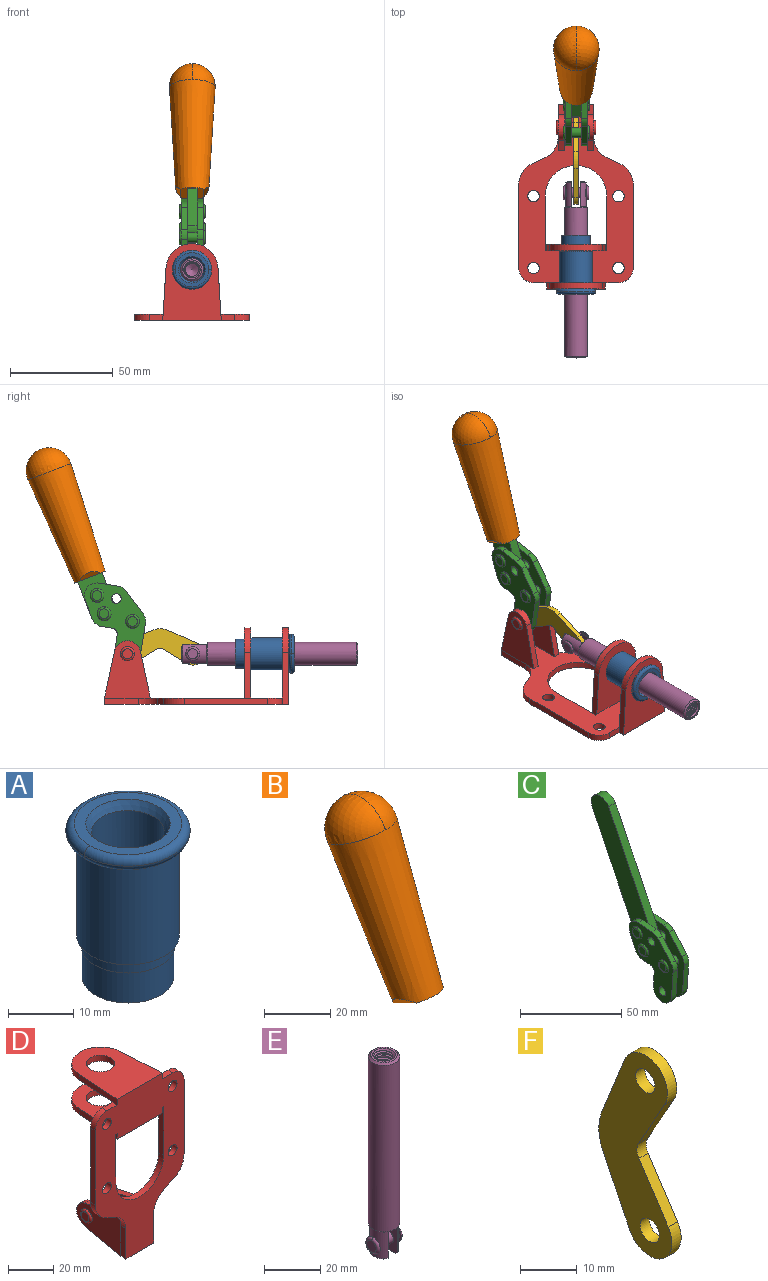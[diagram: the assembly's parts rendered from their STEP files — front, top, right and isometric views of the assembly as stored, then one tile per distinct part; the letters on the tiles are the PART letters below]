
ASSEMBLY  parts=6 mates=6
PART A: 15 faces, bbox 20.6x20.6x28.7 mm
  f0: torus R=8.26mm, axis (0,0,1), area 56.8mm2, adj f1,f10,f12
  f1: torus R=8.26mm, axis (0,0,1), area 56.8mm2, adj f0,f6,f13
  f2: cylinder r=5.59mm len=25.91mm, axis (0,0,1), area 909.6mm2, adj f3,f4
  f3: cone r=6.86mm half-angle=45deg, axis (0,0,-1), area 70.2mm2, adj f2,f14
  f4: cone r=6.47mm half-angle=30deg, axis (0,0,1), area 66.7mm2, adj f2,f13
  f5: cylinder r=7.04mm len=14.07mm, axis (0,0,1), area 252.6mm2, adj f11,f14
  f6: torus R=8.26mm, axis (0,0,1), area 56.8mm2, adj f1,f12,f13
  f7: cylinder r=7.16mm len=14.33mm, axis (0,0,1), area 91.5mm2, adj f9,f11
  f8: cylinder r=7.86mm len=18.42mm, axis (0,0,1), area 909.6mm2, adj f9,f10
  f9: plane 15.72x15.72mm, normal (0,0,-1), area 33mm2, adj f7,f8
  f10: plane 16.51x16.51mm, normal (0,0,-1), area 19.9mm2, adj f0,f8,f12
  f11: plane 14.33x14.33mm, normal (0,0,-1), area 5.7mm2, adj f5,f7
  f12: torus R=8.26mm, axis (0,0,1), area 56.8mm2, adj f0,f6,f10
  f13: plane 16.51x16.51mm, normal (0,0,1), area 82.7mm2, adj f1,f4,f6
  f14: plane 14.07x14.07mm, normal (0,0,-1), area 7.8mm2, adj f3,f5
PART B: 11 faces, bbox 22.3x42.6x64.5 mm
  f0: sphere r=11.13mm, area 411.4mm2, adj f1,f8
  f1: cone r=11.11mm half-angle=3.3deg, axis (0,0.44,0.9), area 3251.8mm2, adj f0,f7,f8,f9,f10
  f2: cylinder r=6.16mm len=11.7mm, axis (1,0,0), area 89.5mm2, adj f3,f4,f5,f6
  f3: plane 60.23x36.75mm, normal (-1,0,0), area 763.6mm2, adj f2,f4,f6,f10
  f4: plane 51.37x25.05mm, normal (0,0.9,-0.44), area 264.2mm2, adj f2,f3,f5,f10
  f5: plane 60.23x36.75mm, normal (1,0,0), area 763.6mm2, adj f2,f4,f6,f10
  f6: plane 51.37x25.05mm, normal (0,-0.9,0.44), area 264.2mm2, adj f2,f3,f5,f10
  f7: plane 9.95x5.95mm, normal (0.71,-0.31,-0.64), area 25.8mm2, adj f1,f10
  f8: sphere r=11.13mm, area 411.4mm2, adj f0,f1
  f9: plane 9.95x5.95mm, normal (-0.71,-0.31,-0.64), area 25.8mm2, adj f1,f10
  f10: plane 14.27x11.38mm, normal (0,-0.44,-0.9), area 106.7mm2, adj f1,f3,f4,f5,f6,f7,f9
PART C: 59 faces, bbox 12.9x60.2x99.6 mm
  f0: torus R=2.39mm, axis (-1,0,0), area 14.9mm2, adj f20,f43,f51
  f1: torus R=2.39mm, axis (-1,0,0), area 14.9mm2, adj f19,f42,f51
  f2: torus R=2.39mm, axis (-1,0,0), area 14.9mm2, adj f18,f35,f51
  f3: torus R=2.39mm, axis (-1,0,0), area 14.9mm2, adj f14,f17,f23
  f4: torus R=2.39mm, axis (-1,0,0), area 14.9mm2, adj f13,f16,f23
  f5: torus R=2.39mm, axis (-1,0,0), area 14.9mm2, adj f12,f15,f23
  f6: cylinder r=2.39mm len=4.78mm, axis (1,0,0), area 46.5mm2, adj f48,f50,f51
  f7: cylinder r=2.39mm len=4.78mm, axis (1,0,0), area 46.5mm2, adj f50,f51
  f8: cylinder r=6.35mm len=12.68mm, axis (1,0,0), area 61.8mm2, adj f38,f39,f50,f51
  f9: cylinder r=2.39mm len=4.78mm, axis (-1,0,0), area 70.5mm2, adj f46,f50
  f10: cylinder r=2.39mm len=4.78mm, axis (-1,0,0), area 46.5mm2, adj f23,f45,f46
  f11: cylinder r=2.39mm len=4.78mm, axis (-1,0,0), area 46.5mm2, adj f23,f46
  f12: plane 4.78x4.78mm, normal (1,0,0), area 17.9mm2, adj f5,f15
  f13: plane 4.78x4.78mm, normal (1,0,0), area 17.9mm2, adj f4,f16
  f14: plane 4.78x4.78mm, normal (1,0,0), area 17.9mm2, adj f3,f17
  f15: torus R=2.39mm, axis (-1,0,0), area 14.9mm2, adj f5,f12,f23
  f16: torus R=2.39mm, axis (-1,0,0), area 14.9mm2, adj f4,f13,f23
  f17: torus R=2.39mm, axis (-1,0,0), area 14.9mm2, adj f3,f14,f23
  f18: plane 4.78x4.78mm, normal (-1,0,0), area 17.9mm2, adj f2,f35
  f19: plane 4.78x4.78mm, normal (-1,0,0), area 17.9mm2, adj f1,f42
  f20: plane 4.78x4.78mm, normal (-1,0,0), area 17.9mm2, adj f0,f43
  f21: plane 2.26x0.2mm, normal (1,0,0), area 0.2mm2, adj f31,f44
  f22: plane 2.26x0.2mm, normal (-1,0,0), area 0.2mm2, adj f41,f44
  f23: plane 39.37x30.77mm, normal (1,0,0), area 565.5mm2, adj f3,f4,f5,f10,f11,f15,f16,f17
  f24: cylinder r=6.1mm len=4.15mm, axis (-1,0,0), area 14.7mm2, adj f23,f25,f32,f46
  f25: plane 10.25x9.01mm, normal (0,-0.75,0.66), area 42.3mm2, adj f23,f24,f26,f46
  f26: cylinder r=6.35mm len=4.64mm, axis (-1,0,0), area 15.6mm2, adj f23,f25,f27,f46
  f27: plane 15.84x3.1mm, normal (0,-1,-0.07), area 49.2mm2, adj f23,f26,f28,f46
  f28: cylinder r=6.35mm len=12.68mm, axis (-1,0,0), area 61.8mm2, adj f23,f27,f29,f46
  f29: plane 8.11x3.1mm, normal (0,1,0.07), area 25.2mm2, adj f23,f28,f30,f46
  f30: cylinder r=3.05mm len=3.25mm, axis (-1,0,0), area 14.8mm2, adj f23,f29,f31,f46
  f31: plane 5.99x3.1mm, normal (0,0.07,-1), area 18.6mm2, adj f21,f23,f30,f44,f46
  f32: plane 9.5x3.1mm, normal (0,-0.07,1), area 29.5mm2, adj f23,f24,f33,f46,f47
  f33: cylinder r=6.1mm len=8.63mm, axis (-1,0,0), area 39.1mm2, adj f23,f32,f34,f47
  f34: plane 8.65x3.96mm, normal (0,0.91,-0.42), area 29.5mm2, adj f23,f33,f44,f47
  f35: torus R=2.39mm, axis (-1,0,0), area 14.9mm2, adj f2,f18,f51
  f36: plane 10.25x9.01mm, normal (0,-0.75,0.66), area 42.3mm2, adj f37,f49,f50,f51
  f37: cylinder r=6.35mm len=4.64mm, axis (1,0,0), area 15.6mm2, adj f36,f38,f50,f51
  f38: plane 15.84x3.1mm, normal (0,-1,-0.07), area 49.2mm2, adj f8,f37,f50,f51
  f39: plane 8.11x3.1mm, normal (0,1,0.07), area 25.2mm2, adj f8,f40,f50,f51
  f40: cylinder r=3.05mm len=3.25mm, axis (1,0,0), area 14.8mm2, adj f39,f41,f50,f51
  f41: plane 5.99x3.1mm, normal (0,0.07,-1), area 18.6mm2, adj f22,f40,f44,f50,f51
  f42: torus R=2.39mm, axis (-1,0,0), area 14.9mm2, adj f1,f19,f51
  f43: torus R=2.39mm, axis (-1,0,0), area 14.9mm2, adj f0,f20,f51
  f44: cylinder r=6.35mm len=12.12mm, axis (-1,0,0), area 128.9mm2, adj f21,f22,f23,f31,f34,f41,f46,f47
  f45: plane 2.65x1.35mm, normal (1,0,0), area 1mm2, adj f10,f55
  f46: plane 39.08x20.42mm, normal (-1,0,0), area 412.5mm2, adj f9,f10,f11,f24,f25,f26,f27,f28
  f47: plane 77.62x39.82mm, normal (1,0,0), area 850mm2, adj f32,f33,f34,f44,f53,f54,f55
  f48: plane 2.65x1.35mm, normal (-1,0,0), area 1mm2, adj f6,f55
  f49: cylinder r=6.1mm len=4.15mm, axis (1,0,0), area 14.7mm2, adj f36,f50,f51,f56
  f50: plane 39.08x20.42mm, normal (1,0,0), area 412.5mm2, adj f6,f7,f8,f9,f36,f37,f38,f39
  f51: plane 39.37x30.77mm, normal (-1,0,0), area 565.5mm2, adj f0,f1,f2,f6,f7,f8,f35,f36
  f52: plane 8.65x3.96mm, normal (0,0.91,-0.42), area 29.5mm2, adj f44,f51,f57,f58
  f53: plane 68.49x33.4mm, normal (0,0.9,-0.44), area 358.1mm2, adj f44,f47,f54,f58
  f54: cylinder r=6.35mm len=12.06mm, axis (1,0,0), area 93.7mm2, adj f47,f53,f55,f58
  f55: plane 68.49x33.4mm, normal (0,-0.9,0.44), area 358.1mm2, adj f44,f45,f46,f47,f48,f50,f54,f58
  f56: plane 9.5x3.1mm, normal (0,-0.07,1), area 29.5mm2, adj f49,f50,f51,f57,f58
  f57: cylinder r=6.1mm len=8.63mm, axis (1,0,0), area 39.1mm2, adj f51,f52,f56,f58
  f58: plane 77.62x39.82mm, normal (-1,0,0), area 850mm2, adj f44,f52,f53,f54,f55,f56,f57
PART D: 55 faces, bbox 55.7x37.4x89.8 mm
  f0: torus R=2.41mm, axis (-1,0,0), area 15mm2, adj f11,f15,f25
  f1: torus R=2.41mm, axis (-1,0,0), area 15mm2, adj f10,f12,f22
  f2: cylinder r=2.78mm len=5.56mm, axis (0,-1,0), area 54.2mm2, adj f30,f54
  f3: cylinder r=14.99mm len=29.97mm, axis (0,-1,0), area 145.9mm2, adj f30,f49,f53,f54
  f4: cylinder r=2.78mm len=5.56mm, axis (0,-1,0), area 54.2mm2, adj f30,f54
  f5: cylinder r=2.78mm len=5.56mm, axis (0,-1,0), area 54.2mm2, adj f30,f54
  f6: cylinder r=2.78mm len=5.56mm, axis (0,-1,0), area 54.2mm2, adj f30,f54
  f7: cylinder r=6.35mm len=12.7mm, axis (0,0,1), area 123.6mm2, adj f27,f51
  f8: cylinder r=6.35mm len=12.7mm, axis (0,0,-1), area 124.7mm2, adj f21,f35
  f9: cylinder r=2.41mm len=11.18mm, axis (-1,0,0), area 169.4mm2, adj f16,f19
  f10: plane 4.83x4.83mm, normal (1,0,0), area 18.3mm2, adj f1,f12
  f11: plane 4.83x4.83mm, normal (-1,0,0), area 18.3mm2, adj f0,f15
  f12: torus R=2.41mm, axis (-1,0,0), area 15mm2, adj f1,f10,f22
  f13: cylinder r=6.35mm len=12.41mm, axis (1,0,0), area 53.4mm2, adj f18,f19,f22,f23
  f14: cylinder r=6.35mm len=12.41mm, axis (-1,0,0), area 53.4mm2, adj f16,f17,f24,f25
  f15: torus R=2.41mm, axis (-1,0,0), area 15mm2, adj f0,f11,f25
  f16: plane 27.86x22.35mm, normal (1,0,0), area 425.4mm2, adj f9,f14,f17,f24,f30
  f17: plane 22.86x4.97mm, normal (0,0.21,0.98), area 72.5mm2, adj f14,f16,f25,f30
  f18: plane 22.86x4.97mm, normal (0,0.21,0.98), area 72.5mm2, adj f13,f19,f22,f30
  f19: plane 27.86x22.35mm, normal (-1,0,0), area 425.4mm2, adj f9,f13,f18,f23,f30
  f20: cylinder r=12.7mm len=25.35mm, axis (0,0,-1), area 119.8mm2, adj f21,f34,f35,f36
  f21: plane 34.21x28.07mm, normal (0,0,-1), area 702.4mm2, adj f8,f20,f30,f34,f36
  f22: plane 27.96x22.45mm, normal (1,0,0), area 407.2mm2, adj f1,f12,f13,f18,f23,f30,f42,f43
  f23: plane 22.86x4.97mm, normal (0,0.21,-0.98), area 72.5mm2, adj f13,f19,f22,f44
  f24: plane 22.86x4.97mm, normal (0,0.21,-0.98), area 72.5mm2, adj f14,f16,f25,f44
  f25: plane 27.86x22.35mm, normal (-1,0,0), area 407.1mm2, adj f0,f14,f15,f17,f24,f30,f45,f46
  f26: plane 3.1x0.95mm, normal (0,0,-1), area 2.7mm2, adj f30,f49,f50,f54
  f27: plane 34.21x28.07mm, normal (0,0,1), area 702.4mm2, adj f7,f28,f30,f50,f52
  f28: cylinder r=12.7mm len=25.35mm, axis (0,0,1), area 118.8mm2, adj f27,f50,f51,f52
  f29: plane 3.1x0.95mm, normal (0,0,-1), area 2.7mm2, adj f30,f52,f53,f54
  f30: plane 86.54x55.63mm, normal (0,1,0), area 2362.9mm2, adj f2,f3,f4,f5,f6,f16,f17,f18
  f31: plane 40.56x3.1mm, normal (-1,0,0), area 125.7mm2, adj f30,f32,f48,f54
  f32: cylinder r=7.11mm len=7.11mm, axis (0,-1,0), area 34.6mm2, adj f30,f31,f33,f54
  f33: plane 6.67x3.1mm, normal (0,0,1), area 20.4mm2, adj f30,f32,f34,f54
  f34: plane 25.39x3.13mm, normal (-1,0.06,0), area 79.5mm2, adj f20,f21,f33,f35,f54
  f35: plane 37.31x28.45mm, normal (0,0,1), area 789.9mm2, adj f8,f20,f34,f36,f54
  f36: plane 25.39x3.13mm, normal (1,0.06,0), area 79.5mm2, adj f20,f21,f35,f37,f54
  f37: plane 6.67x3.1mm, normal (0,0,1), area 20.4mm2, adj f30,f36,f38,f54
  f38: cylinder r=7.11mm len=7.11mm, axis (0,-1,0), area 34.6mm2, adj f30,f37,f39,f54
  f39: plane 40.56x3.1mm, normal (1,0,0), area 125.7mm2, adj f30,f38,f40,f54
  f40: cylinder r=11.18mm len=10.16mm, axis (0,-1,0), area 39.5mm2, adj f30,f39,f41,f54
  f41: plane 6.09x3.1mm, normal (0.42,0,-0.91), area 20.8mm2, adj f30,f40,f42,f54
  f42: cylinder r=11.18mm len=9.41mm, axis (0,-1,0), area 37.2mm2, adj f22,f30,f41,f43,f54
  f43: plane 16.5x3.1mm, normal (1,0,0), area 51.1mm2, adj f22,f42,f44,f54
  f44: plane 17.37x3.1mm, normal (0,0,-1), area 53.8mm2, adj f23,f24,f30,f43,f45,f54
  f45: plane 16.5x3.1mm, normal (-1,0,0), area 51.1mm2, adj f25,f44,f46,f54
  f46: cylinder r=11.18mm len=9.41mm, axis (0,-1,0), area 37.2mm2, adj f25,f30,f45,f47,f54
  f47: plane 6.09x3.1mm, normal (-0.42,0,-0.91), area 20.8mm2, adj f30,f46,f48,f54
  f48: cylinder r=11.18mm len=10.16mm, axis (0,-1,0), area 39.5mm2, adj f30,f31,f47,f54
  f49: plane 26.54x3.1mm, normal (-1,0,0), area 82.3mm2, adj f3,f26,f30,f54
  f50: plane 25.39x3.1mm, normal (1,0.06,0), area 78.8mm2, adj f26,f27,f28,f51,f54
  f51: plane 37.31x28.45mm, normal (0,0,-1), area 789.9mm2, adj f7,f28,f50,f52,f54
  f52: plane 25.39x3.1mm, normal (-1,0.06,0), area 78.8mm2, adj f27,f28,f29,f51,f54
  f53: plane 26.54x3.1mm, normal (1,0,0), area 82.3mm2, adj f3,f29,f30,f54
  f54: plane 89.66x55.63mm, normal (0,-1,0), area 2678.5mm2, adj f2,f3,f4,f5,f6,f26,f29,f31
PART E: 48 faces, bbox 12.6x11.1x86.1 mm
  f0: torus R=2.41mm, axis (-1,0,0), area 15mm2, adj f30,f32,f34
  f1: torus R=2.41mm, axis (-1,0,0), area 15mm2, adj f29,f31,f33
  f2: cylinder r=5.54mm len=72.39mm, axis (0,0,1), area 2518.5mm2, adj f3,f4,f42,f43
  f3: cone r=5.54mm half-angle=45deg, axis (0,0,1), area 7.6mm2, adj f2,f5,f41
  f4: cone r=5.54mm half-angle=45deg, axis (0,0,-1), area 34.9mm2, adj f2,f39
  f5: cylinder r=5.08mm len=11.48mm, axis (0,0,1), area 108.3mm2, adj f3,f7,f8,f41
  f6: cylinder r=2.41mm len=4.83mm, axis (-1,0,0), area 71.2mm2, adj f40,f41
  f7: cylinder r=2.41mm len=4.83mm, axis (-1,0,0), area 7.6mm2, adj f5,f34
  f8: cone r=5.08mm half-angle=45deg, axis (0,0,1), area 10.6mm2, adj f5,f37,f41
  f9: cone r=3.98mm half-angle=45deg, axis (0,0,1), area 17.6mm2, adj f27,f39,f45,f46,f47
  f10: cylinder r=2.41mm len=4.83mm, axis (-1,0,0), area 7.6mm2, adj f33,f38
  f11: cylinder r=3.2mm len=6.4mm, axis (0,0,1), area 78.4mm2, adj f12,f28,f44,f45,f47
  f12: cylinder r=3.2mm len=6.4mm, axis (0,0,1), area 10.5mm2, adj f11,f13,f45,f47
  f13: cylinder r=3.2mm len=6.4mm, axis (0,0,1), area 10.5mm2, adj f12,f14,f45,f47
  f14: cylinder r=3.2mm len=6.4mm, axis (0,0,1), area 10.5mm2, adj f13,f15,f45,f47
  f15: cylinder r=3.2mm len=6.4mm, axis (0,0,1), area 10.5mm2, adj f14,f16,f45,f47
  f16: cylinder r=3.2mm len=6.4mm, axis (0,0,1), area 10.5mm2, adj f15,f17,f45,f47
  f17: cylinder r=3.2mm len=6.4mm, axis (0,0,1), area 10.5mm2, adj f16,f18,f45,f47
  f18: cylinder r=3.2mm len=6.4mm, axis (0,0,1), area 10.5mm2, adj f17,f19,f45,f47
  f19: cylinder r=3.2mm len=6.4mm, axis (0,0,1), area 10.5mm2, adj f18,f20,f45,f47
  f20: cylinder r=3.2mm len=6.4mm, axis (0,0,1), area 10.5mm2, adj f19,f21,f45,f47
  f21: cylinder r=3.2mm len=6.4mm, axis (0,0,1), area 10.5mm2, adj f20,f22,f45,f47
  f22: cylinder r=3.2mm len=6.4mm, axis (0,0,1), area 10.5mm2, adj f21,f23,f45,f47
  f23: cylinder r=3.2mm len=6.4mm, axis (0,0,1), area 10.5mm2, adj f22,f24,f45,f47
  f24: cylinder r=3.2mm len=6.4mm, axis (0,0,1), area 10.5mm2, adj f23,f25,f45,f47
  f25: cylinder r=3.2mm len=6.4mm, axis (0,0,1), area 10.5mm2, adj f24,f26,f45,f47
  f26: cylinder r=3.2mm len=6.4mm, axis (0,0,1), area 10.5mm2, adj f25,f27,f45,f47
  f27: cylinder r=3.2mm len=6.4mm, axis (0,0,1), area 7.4mm2, adj f9,f26,f45,f47
  f28: cone r=3.2mm half-angle=60deg, axis (0,0,1), area 37.2mm2, adj f11
  f29: plane 4.83x4.83mm, normal (-1,0,0), area 18.3mm2, adj f1,f31
  f30: plane 4.83x4.83mm, normal (1,0,0), area 18.3mm2, adj f0,f32
  f31: torus R=2.41mm, axis (-1,0,0), area 15mm2, adj f1,f29,f33
  f32: torus R=2.41mm, axis (-1,0,0), area 15mm2, adj f0,f30,f34
  f33: plane 6.83x6.83mm, normal (1,0,0), area 18.3mm2, adj f1,f10,f31
  f34: plane 6.83x6.83mm, normal (-1,0,0), area 18.3mm2, adj f0,f7,f32
  f35: cone r=5.08mm half-angle=45deg, axis (0,0,1), area 10.6mm2, adj f36,f38,f40
  f36: plane 7.25x1.97mm, normal (0,0,-1), area 10mm2, adj f35,f40
  f37: plane 7.25x1.97mm, normal (0,0,-1), area 10mm2, adj f8,f41
  f38: cylinder r=5.08mm len=11.48mm, axis (0,0,1), area 108.3mm2, adj f10,f35,f40,f42
  f39: plane 9.55x9.55mm, normal (0,0,1), area 22mm2, adj f4,f9
  f40: plane 12.76x10.09mm, normal (1,0,0), area 95.7mm2, adj f6,f35,f36,f38,f42,f43
  f41: plane 12.76x10.09mm, normal (-1,0,0), area 95.7mm2, adj f3,f5,f6,f8,f37,f43
  f42: cone r=5.54mm half-angle=45deg, axis (0,0,1), area 7.6mm2, adj f2,f38,f40
  f43: plane 11.07x4.7mm, normal (0,0,-1), area 50.4mm2, adj f2,f40,f41
  f44: plane 0.89x0.62mm, normal (-1,0,0), area 0.3mm2, adj f11,f45,f46,f47
  f45: bspline ~24.8x7.63mm, area 266.6mm2, adj f9,f11,f12,f13,f14,f15,f16,f17
  f46: bspline ~24.87x7.63mm, area 73.6mm2, adj f9,f44,f45,f47
  f47: bspline ~24.98x7.63mm, area 272.5mm2, adj f9,f11,f12,f13,f14,f15,f16,f17
PART F: 12 faces, bbox 2.3x18.2x42.8 mm
  f0: cylinder r=2.4mm len=4.8mm, axis (1,0,0), area 34.9mm2, adj f4,f11
  f1: cylinder r=10.41mm len=8.47mm, axis (1,0,0), area 20.2mm2, adj f4,f9,f10,f11
  f2: cylinder r=3.05mm len=3.16mm, axis (1,0,0), area 7.7mm2, adj f4,f6,f7,f11
  f3: cylinder r=2.4mm len=4.8mm, axis (1,0,0), area 34.9mm2, adj f4,f11
  f4: plane 42.81x18.23mm, normal (-1,0,0), area 414.1mm2, adj f0,f1,f2,f3,f5,f6,f7,f8
  f5: cylinder r=5.54mm len=10.67mm, axis (1,0,0), area 41.8mm2, adj f4,f6,f10,f11
  f6: plane 11.66x6.53mm, normal (0,-0.87,-0.49), area 30.9mm2, adj f2,f4,f5,f11
  f7: plane 11.17x7.33mm, normal (0,-0.84,0.55), area 30.9mm2, adj f2,f4,f8,f11
  f8: cylinder r=5.54mm len=10.51mm, axis (1,0,0), area 41.8mm2, adj f4,f7,f9,f11
  f9: plane 13.67x6.67mm, normal (0,0.9,-0.44), area 35.1mm2, adj f1,f4,f8,f11
  f10: plane 14.1x5.7mm, normal (0,0.93,0.37), area 35.1mm2, adj f1,f4,f5,f11
  f11: plane 42.81x18.23mm, normal (1,0,0), area 414.1mm2, adj f0,f1,f2,f3,f5,f6,f7,f8
PLACE A rot(axis=(1,0,0),90deg) t=(0,0,0)mm
PLACE B rot(axis=(1,0,0),5deg) t=(0.14,4.78,54.44)mm
PLACE C rot(axis=(1,0,0),5deg) t=(0.14,4.78,54.44)mm
PLACE D rot(axis=(1,0,0),90deg) t=(0,0,0)mm fixed
PLACE E rot(axis=(1,0,0),90deg) t=(0,15.82,0)mm
PLACE F rot(axis=(0,0.72,0.69),180deg) t=(0,15.77,0.55)mm
MATE fastened B.f2 <-> C.f54  axis (1,0,0) through (0.14,70.77,115.19)mm
MATE revolute F.f5 <-> D.f0  axis (-1,0,0) through (0,32.09,24.61)mm
MATE fastened A.f2 <-> D.f7  axis (0,1,0) through (0,-46.39,24.61)mm
MATE revolute F.f3 <-> E.f6  axis (-1,0,0) through (0,0.34,24.61)mm
MATE revolute C.f7 <-> D.f0  axis (1,0,0) through (5.59,32.09,24.61)mm
MATE slider E.f2 <-> A.f2  axis (0,-1,0) through (0,-42.96,24.61)mm
